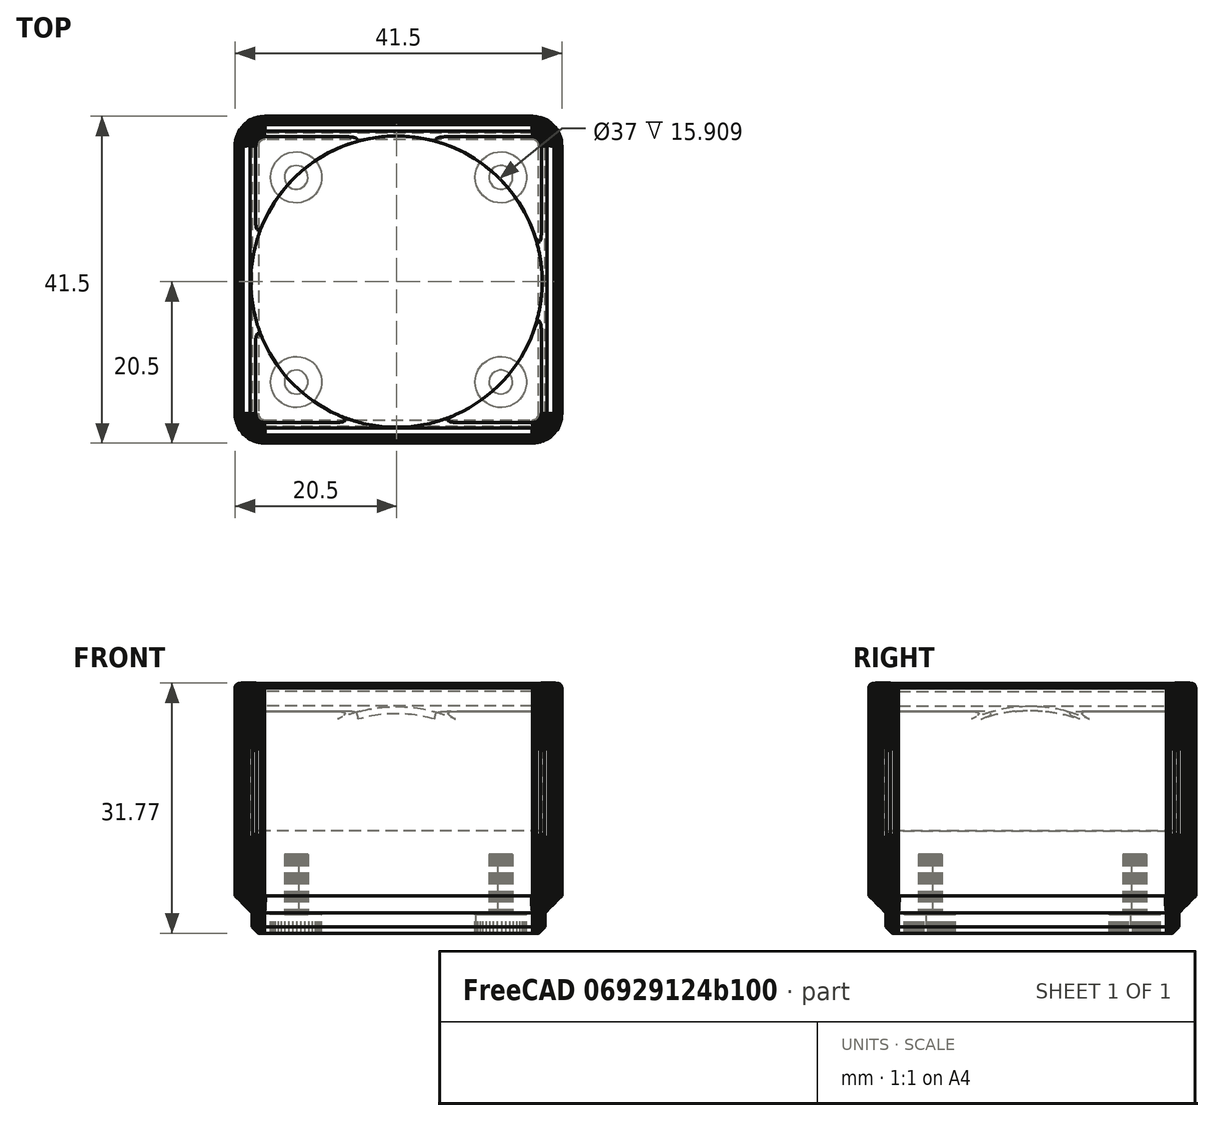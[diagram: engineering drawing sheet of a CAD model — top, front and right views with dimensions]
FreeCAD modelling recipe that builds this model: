
FCSTD DOCUMENT  (FreeCAD 0.20R29410 (Git))
Label: 1x1_37mm
License: All rights reserved
LicenseURL: http://en.wikipedia.org/wiki/All_rights_reserved
objects: Part::Feature×2, Mesh::Feature×1, Part::Refine×1, PartDesign::FeatureBase×1, Sketcher::SketchObject×1, PartDesign::Pocket×1, PartDesign::Fillet×1, PartDesign::Body×1
note: 10 computed .brp shape members not serialized (recipe doc carries the construction recipe); baked Part::Feature solids carry a one-line shape summary decoded from their .brp

FEATURE [Mesh::Feature] _x1_Block_1_25in  label="1x1 Block 1.25in"
FEATURE [Part::Feature] _x1_Block_1_25in001
  shape: bbox 41.5 x 41.5 x 31.77 mm, 5878 faces, 0 solids (baked)
FEATURE [Part::Refine] _x1_Block_1_25in001001
  Source = -> _x1_Block_1_25in001
FEATURE [Part::Feature] _x1_Block_1_25in001001_solid  label="_x1_Block_1_25in001001 (Solid)"
  shape: bbox 41.5 x 41.5 x 31.77 mm, 4300 faces (baked)
FEATURE [PartDesign::FeatureBase] BaseFeature
  BaseFeature = -> _x1_Block_1_25in001001_solid
FEATURE [Sketcher::SketchObject] Sketch
  AttachmentOffset = pos=(0,0,29) rot=(0,0,1;0rad)
  FullyConstrained = true
  MapMode = 5
  Placement = pos=(0,0,29) rot=(0,0,1;0rad)
  Support = -> [XY_Plane]
  expr: Constraints[1] = (41.5 - 37) / 2 + 37 / 2
  expr: Constraints[2] = (41.5 - 37) / 2 + 37 / 2
  sketch-geometry (1):
    g0: Circle CenterX=20.75 CenterY=20.75 CenterZ=0 NormalX=0 NormalY=0 NormalZ=1 AngleXU=0 Radius=18.5
  constraints (3):
    c: Diameter(g0) = 37
    c: DistanceX(g-1,g0) = 20.75
    c: DistanceY(g-1,g0) = 20.75
FEATURE [PartDesign::Pocket] Pocket
  BaseFeature = -> BaseFeature
  Direction = (0,0,-1)
  Length = 16
  Length2 = 5
  Profile = -> Sketch
  ReferenceAxis = -> Sketch [N_Axis]
  Type = 0
FEATURE [PartDesign::Fillet] Fillet
  Base = -> Pocket [Edge4606,Edge4605,Edge4604,Edge4608,Edge4596]
  BaseFeature = -> Pocket
  Radius = 1
  SupportTransform = false
  UseAllEdges = false
FEATURE [PartDesign::Body] Body
  BaseFeature = -> _x1_Block_1_25in001001_solid
  Group = -> [BaseFeature,Sketch,Pocket,Fillet]
  Origin = -> Origin
  Tip = -> Fillet
